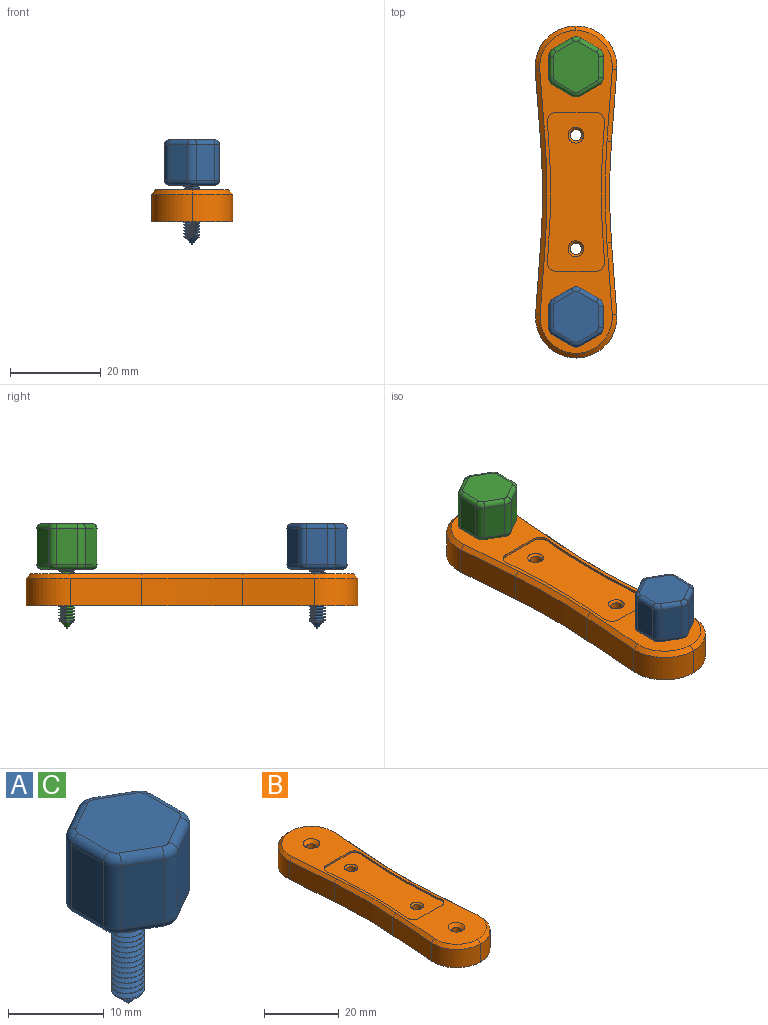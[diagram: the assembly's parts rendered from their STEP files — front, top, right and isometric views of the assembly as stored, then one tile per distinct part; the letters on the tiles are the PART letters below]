
ASSEMBLY  parts=3 mates=2
PART A: 46 faces, bbox 12.3x13.6x23 mm
  f0: cylinder r=1.75mm len=11.3mm, axis (0,0,1), area 23.3mm2, adj f9,f40,f42,f43,f44
  f1: plane 0.1x0.1mm, normal (0,0,-1), area 0mm2, adj f45
  f2: plane 8x4mm, normal (0.5,0.87,0), area 37mm2, adj f10,f11,f24,f38
  f3: plane 8x4mm, normal (-0.5,0.87,0), area 37mm2, adj f11,f12,f27,f34
  f4: plane 8x4.62mm, normal (-1,0,0), area 37mm2, adj f12,f13,f23,f30
  f5: plane 8x4mm, normal (-0.5,-0.87,0), area 37mm2, adj f13,f14,f19,f29
  f6: plane 8x4mm, normal (0.5,-0.87,0), area 37mm2, adj f14,f15,f16,f33
  f7: plane 8x4.62mm, normal (1,0,0), area 37mm2, adj f10,f15,f20,f37
  f8: plane 11.24x10mm, normal (0,0,1), area 86.3mm2, adj f28,f29,f30,f31,f32,f33,f34,f35
  f9: plane 11.24x10mm, normal (0,0,-1), area 76.7mm2, adj f0,f16,f17,f18,f19,f20,f21,f22
  f10: cylinder r=2mm len=8mm, axis (0,0,-1), area 16.8mm2, adj f2,f7,f22,f39
  f11: cylinder r=2mm len=8mm, axis (0,0,-1), area 16.8mm2, adj f2,f3,f26,f36
  f12: cylinder r=2mm len=8mm, axis (0,0,-1), area 16.8mm2, adj f3,f4,f25,f32
  f13: cylinder r=2mm len=8mm, axis (0,0,-1), area 16.8mm2, adj f4,f5,f21,f28
  f14: cylinder r=2mm len=8mm, axis (0,0,-1), area 16.8mm2, adj f5,f6,f17,f31
  f15: cylinder r=2mm len=8mm, axis (0,0,-1), area 16.8mm2, adj f6,f7,f18,f35
  f16: cylinder r=1mm len=4.5mm, axis (0.87,0.5,0), area 7.3mm2, adj f6,f9,f17,f18
  f17: torus R=1mm, axis (0,0,1), area 2.7mm2, adj f9,f14,f16,f19
  f18: torus R=1mm, axis (0,0,1), area 2.7mm2, adj f9,f15,f16,f20
  f19: cylinder r=1mm len=4.5mm, axis (0.87,-0.5,0), area 7.3mm2, adj f5,f9,f17,f21
  f20: cylinder r=1mm len=4.62mm, axis (0,1,0), area 7.3mm2, adj f7,f9,f18,f22
  f21: torus R=1mm, axis (0,0,1), area 2.7mm2, adj f9,f13,f19,f23
  f22: torus R=1mm, axis (0,0,1), area 2.7mm2, adj f9,f10,f20,f24
  f23: cylinder r=1mm len=4.62mm, axis (0,-1,0), area 7.3mm2, adj f4,f9,f21,f25
  f24: cylinder r=1mm len=4.5mm, axis (-0.87,0.5,0), area 7.3mm2, adj f2,f9,f22,f26
  f25: torus R=1mm, axis (0,0,1), area 2.7mm2, adj f9,f12,f23,f27
  f26: torus R=1mm, axis (0,0,1), area 2.7mm2, adj f9,f11,f24,f27
  f27: cylinder r=1mm len=4.5mm, axis (-0.87,-0.5,0), area 7.3mm2, adj f3,f9,f25,f26
  f28: torus R=1mm, axis (0,0,1), area 2.7mm2, adj f8,f13,f29,f30
  f29: cylinder r=1mm len=4.5mm, axis (-0.87,0.5,0), area 7.3mm2, adj f5,f8,f28,f31
  f30: cylinder r=1mm len=4.62mm, axis (0,1,0), area 7.3mm2, adj f4,f8,f28,f32
  f31: torus R=1mm, axis (0,0,1), area 2.7mm2, adj f8,f14,f29,f33
  f32: torus R=1mm, axis (0,0,1), area 2.7mm2, adj f8,f12,f30,f34
  f33: cylinder r=1mm len=4.5mm, axis (-0.87,-0.5,0), area 7.3mm2, adj f6,f8,f31,f35
  f34: cylinder r=1mm len=4.5mm, axis (0.87,0.5,0), area 7.3mm2, adj f3,f8,f32,f36
  f35: torus R=1mm, axis (0,0,1), area 2.7mm2, adj f8,f15,f33,f37
  f36: torus R=1mm, axis (0,0,1), area 2.7mm2, adj f8,f11,f34,f38
  f37: cylinder r=1mm len=4.62mm, axis (0,-1,0), area 7.3mm2, adj f7,f8,f35,f39
  f38: cylinder r=1mm len=4.5mm, axis (0.87,-0.5,0), area 7.3mm2, adj f2,f8,f36,f39
  f39: torus R=1mm, axis (0,0,1), area 2.7mm2, adj f8,f10,f37,f38
  f40: plane 0.58x0.5mm, normal (0,1,0), area 0.1mm2, adj f0,f41,f42,f43
  f41: cylinder r=1.75mm len=3.5mm, axis (0,0,1), area 1mm2, adj f9,f40,f43
  f42: bspline ~12.21x4.04mm, area 95.9mm2, adj f0,f40,f43,f44,f45
  f43: bspline ~12.21x4.04mm, area 99mm2, adj f0,f40,f41,f42,f44
  f44: cone r=0.05mm half-angle=45deg, axis (0,0,1), area 1mm2, adj f0,f42,f43,f45
  f45: cone r=0.05mm half-angle=45deg, axis (0,0,1), area 9.5mm2, adj f1,f42,f44
PART B: 45 faces, bbox 18x73x7 mm
  f0: cone r=2.25mm half-angle=45deg, axis (0,0,1), area 6.7mm2, adj f16,f44
  f1: cone r=2.25mm half-angle=45deg, axis (0,0,1), area 6.7mm2, adj f17,f44
  f2: cylinder r=150mm len=22.26mm, axis (0,0,-1), area 133.7mm2, adj f3,f11,f13,f22
  f3: plane 15.7x6mm, normal (1,-0.07,0), area 94.5mm2, adj f2,f4,f13,f20
  f4: cylinder r=9mm len=9.67mm, axis (0,0,-1), area 88.8mm2, adj f3,f5,f13,f21
  f5: cylinder r=9mm len=9.68mm, axis (0,0,-1), area 88.8mm2, adj f4,f6,f13,f23
  f6: plane 15.7x6mm, normal (-1,-0.08,0), area 94.5mm2, adj f5,f7,f13,f25
  f7: cylinder r=150mm len=22.26mm, axis (0,0,-1), area 133.7mm2, adj f6,f8,f13,f27
  f8: plane 15.71x6mm, normal (-1,0.07,0), area 94.5mm2, adj f7,f9,f13,f29
  f9: cylinder r=9mm len=9.65mm, axis (0,0,-1), area 88.5mm2, adj f8,f10,f13,f28
  f10: cylinder r=9mm len=9.67mm, axis (0,0,-1), area 88.5mm2, adj f9,f11,f13,f26
  f11: plane 15.7x6mm, normal (1,0.07,0), area 94.5mm2, adj f2,f10,f13,f24
  f12: plane 71x15.99mm, normal (0,0,1), area 533.6mm2, adj f18,f19,f20,f21,f22,f23,f24,f25
  f13: plane 73x17.99mm, normal (0,0,-1), area 1117.1mm2, adj f2,f3,f4,f5,f6,f7,f8,f9
  f14: cylinder r=1.25mm len=6mm, axis (0,0,-1), area 47.1mm2, adj f13,f18
  f15: cylinder r=1.25mm len=6mm, axis (0,0,-1), area 47.1mm2, adj f13,f19
  f16: cylinder r=1.25mm len=6mm, axis (0,0,-1), area 47.1mm2, adj f0,f13
  f17: cylinder r=1.25mm len=6mm, axis (0,0,-1), area 47.1mm2, adj f1,f13
  f18: cone r=2.25mm half-angle=45deg, axis (0,0,1), area 15.6mm2, adj f12,f14
  f19: cone r=2.25mm half-angle=45deg, axis (0,0,1), area 15.6mm2, adj f12,f15
  f20: plane 15.78x2.17mm, normal (0.71,-0.05,0.71), area 22.3mm2, adj f3,f12,f21,f22
  f21: cone r=9mm half-angle=45deg, axis (0,0,-1), area 19.8mm2, adj f4,f12,f20,f23
  f22: cone r=150mm half-angle=45deg, axis (0,0,1), area 31.6mm2, adj f2,f12,f20,f24
  f23: cone r=8mm half-angle=45deg, axis (0,0,-1), area 19.8mm2, adj f5,f12,f21,f25
  f24: plane 15.78x2.16mm, normal (0.71,0.05,0.71), area 22.3mm2, adj f11,f12,f22,f26
  f25: plane 15.78x2.19mm, normal (-0.71,-0.05,0.71), area 22.3mm2, adj f6,f12,f23,f27
  f26: cone r=9mm half-angle=45deg, axis (0,0,-1), area 19.7mm2, adj f10,f12,f24,f28
  f27: cone r=151mm half-angle=45deg, axis (0,0,1), area 31.6mm2, adj f7,f12,f25,f29
  f28: cone r=8mm half-angle=45deg, axis (0,0,-1), area 19.7mm2, adj f9,f12,f26,f29
  f29: plane 15.78x2.14mm, normal (-0.71,0.05,0.71), area 22.3mm2, adj f8,f12,f27,f28
  f30: cylinder r=2mm len=2.17mm, axis (0,0,1), area 1.7mm2, adj f12,f31,f43,f44
  f31: plane 4.32x0.5mm, normal (0,-1,0), area 2.2mm2, adj f12,f30,f32,f44
  f32: plane 4.32x0.5mm, normal (0,-1,0), area 2.2mm2, adj f12,f31,f33,f44
  f33: cylinder r=2mm len=2.17mm, axis (0,0,1), area 1.7mm2, adj f12,f32,f34,f44
  f34: plane 2.52x0.5mm, normal (1,0.09,0), area 1.3mm2, adj f12,f33,f35,f44
  f35: cylinder r=150mm len=25.62mm, axis (0,0,1), area 12.8mm2, adj f12,f34,f36,f44
  f36: plane 2.52x0.5mm, normal (1,-0.09,0), area 1.3mm2, adj f12,f35,f37,f44
  f37: cylinder r=2mm len=2.17mm, axis (0,0,1), area 1.7mm2, adj f12,f36,f38,f44
  f38: plane 4.32x0.5mm, normal (0,1,0), area 2.2mm2, adj f12,f37,f39,f44
  f39: plane 4.32x0.5mm, normal (0,1,0), area 2.2mm2, adj f12,f38,f40,f44
  f40: cylinder r=2mm len=2.17mm, axis (0,0,1), area 1.7mm2, adj f12,f39,f41,f44
  f41: plane 2.52x0.5mm, normal (-1,-0.09,0), area 1.3mm2, adj f12,f40,f42,f44
  f42: cylinder r=150mm len=25.62mm, axis (0,0,1), area 12.8mm2, adj f12,f41,f43,f44
  f43: plane 2.52x0.5mm, normal (-1,0.09,0), area 1.3mm2, adj f12,f30,f42,f44
  f44: plane 35x12.65mm, normal (0,0,1), area 388.5mm2, adj f0,f1,f30,f31,f32,f33,f34,f35
PART C: same geometry as A
PLACE A t=(-9.67,-29.28,14.36)mm
PLACE B t=(-8.68,-1.78,6.36)mm
PLACE C t=(-9.65,25.72,14.36)mm
MATE fastened A.f0 <-> B.f10  axis (0,0,-1) through (-9.67,-29.28,14.36)mm
MATE fastened C.f0 <-> B.f5  axis (0,0,-1) through (-9.65,25.72,14.36)mm
